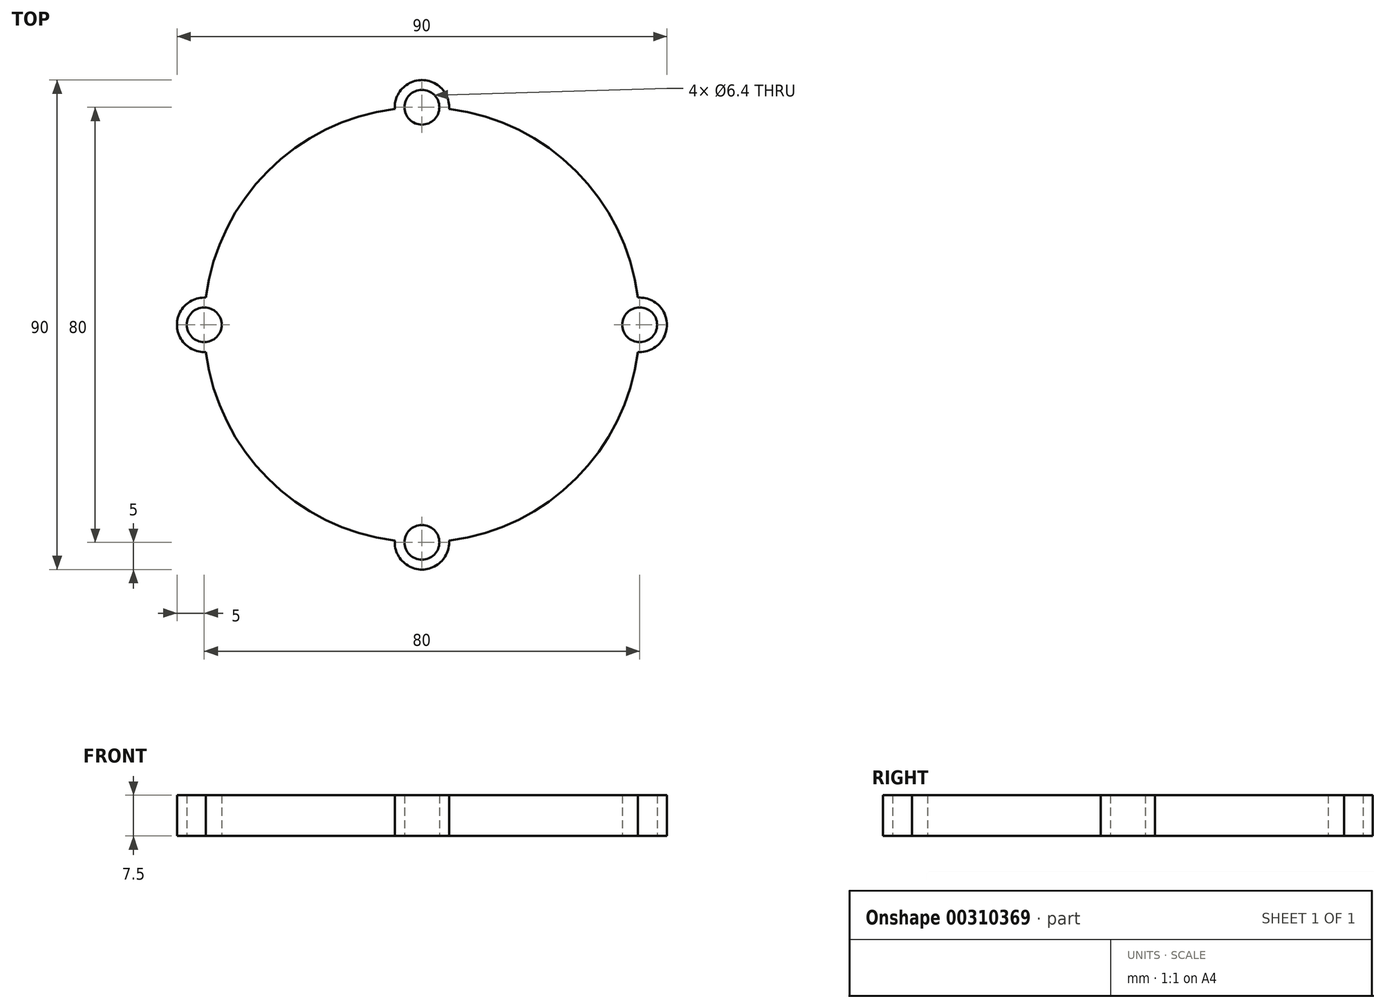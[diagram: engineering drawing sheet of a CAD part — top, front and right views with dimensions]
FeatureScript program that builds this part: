
annotation { "Feature Type Name" : "Feature", "Feature Type Description" : "" }
export const myFeature = defineFeature(function(context is Context, id is Id, definition is map)
    precondition{}
    {
        {
            var Q0;
            Q0=qCreatedBy(makeId("Top.planeOp"),FACE);
            var sketch = newSketch(context, id + "F0", { "sketchPlane" : qUnion([Q0])});
            skCircle(sketch, "E0", {"center": v(0, 0) * mm, "radius": 40 * mm});
            skCircle(sketch, "E1", {"center": v(0, 40) * mm, "radius": 3.2 * mm});
            skCircle(sketch, "E2", {"center": v(-40, 0) * mm, "radius": 3.2 * mm});
            skCircle(sketch, "E3", {"center": v(0, -40) * mm, "radius": 3.2 * mm});
            skCircle(sketch, "E4", {"center": v(40, 0) * mm, "radius": 3.2 * mm});
            skCircle(sketch, "E5", {"center": v(-40, 0) * mm, "radius": 5 * mm});
            skCircle(sketch, "E6", {"center": v(0, 40) * mm, "radius": 5 * mm});
            skCircle(sketch, "E7", {"center": v(40, 0) * mm, "radius": 5 * mm});
            skCircle(sketch, "E8", {"center": v(0, -40) * mm, "radius": 5 * mm});
            skSolve(sketch);
        }
        {
            var Q0;
            Q0 = qSketchRegion(id + "F0", true);
            extrude(context, id + "F1", {"entities" : qUnion([Q0]), "depth" : 7.5 * mm});
        }
    });
